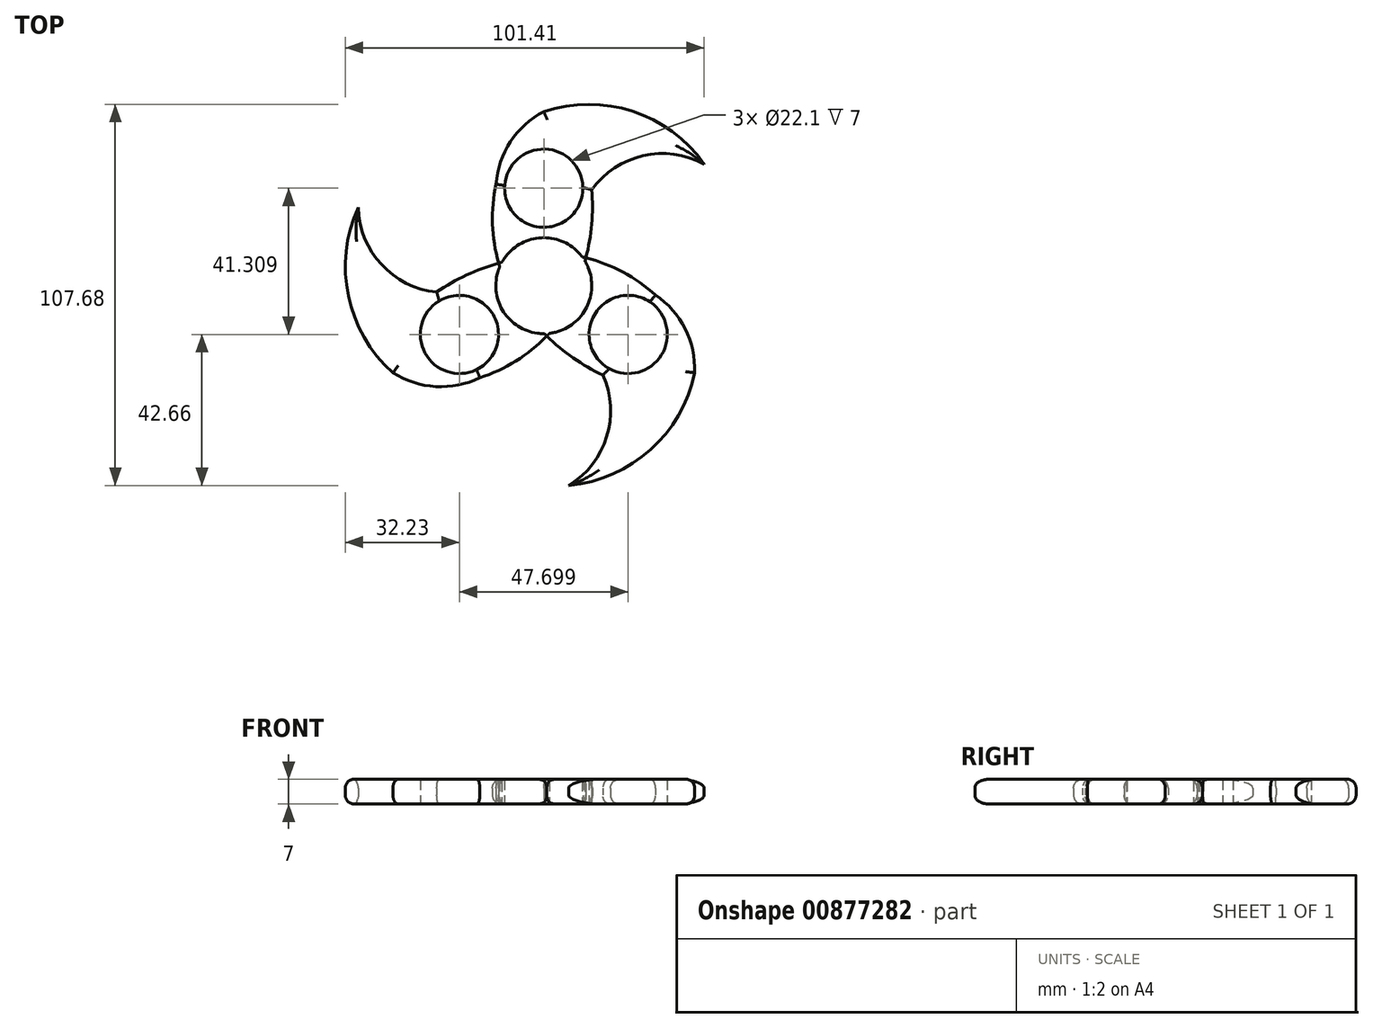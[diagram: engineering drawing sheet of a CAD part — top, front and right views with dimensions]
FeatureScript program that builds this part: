
annotation { "Feature Type Name" : "Feature", "Feature Type Description" : "" }
export const myFeature = defineFeature(function(context is Context, id is Id, definition is map)
    precondition{}
    {
        {
            var Q0;
            Q0=qCreatedBy(makeId("Top.planeOp"),FACE);
            var sketch = newSketch(context, id + "F0", { "sketchPlane" : qUnion([Q0])});
            skCircle(sketch, "E0", {"center": v(0, 0) * mm, "radius": 11.05 * mm});
            skCircle(sketch, "E1", {"center": v(0, 0) * mm, "radius": 13.55 * mm});
            skCircle(sketch, "E2", {"center": v(0, 27.54) * mm, "radius": 11.05 * mm});
            skCircle(sketch, "E3.1.1", {"center": v(-23.85, -13.77) * mm, "radius": 11.05 * mm});
            skCircle(sketch, "E4.2.2.0", {"center": v(23.85, -13.77) * mm, "radius": 11.05 * mm});
            skArc(sketch, "E5", {"start": v(45.33, 34.35) * mm, "mid": v(25.12, 49.26) * mm, "end": v(0, 49.2) * mm});
            skArc(sketch, "E6", {"start": v(45.33, 34.35) * mm, "mid": v(28.07, 36.72) * mm, "end": v(13.54, 27.1) * mm});
            skArc(sketch, "E7", {"start": v(0, 49.2) * mm, "mid": v(-9.43, 40.68) * mm, "end": v(-13.5, 28.65) * mm});
            skArc(sketch, "E8.1.0", {"start": v(-52.41, 22.08) * mm, "mid": v(-55.22, -2.88) * mm, "end": v(-42.6, -24.6) * mm});
            skArc(sketch, "E8.1.1", {"start": v(-52.41, 22.08) * mm, "mid": v(-45.84, 5.94) * mm, "end": v(-30.23, -1.82) * mm});
            skArc(sketch, "E8.2.0", {"start": v(7.08, -56.43) * mm, "mid": v(30.1, -46.39) * mm, "end": v(42.6, -24.6) * mm});
            skArc(sketch, "E8.2.1", {"start": v(7.08, -56.43) * mm, "mid": v(17.77, -42.67) * mm, "end": v(16.7, -25.27) * mm});
            skArc(sketch, "E9.1.0", {"start": v(-42.6, -24.6) * mm, "mid": v(-30.52, -28.5) * mm, "end": v(-18.06, -26.02) * mm});
            skArc(sketch, "E9.2.0", {"start": v(42.6, -24.6) * mm, "mid": v(39.95, -12.18) * mm, "end": v(31.57, -2.63) * mm});
            skArc(sketch, "E10", {"start": v(11.65, 6.92) * mm, "mid": v(13.48, 16.92) * mm, "end": v(13.54, 27.1) * mm});
            skArc(sketch, "E11", {"start": v(-13.5, 28.65) * mm, "mid": v(-14.47, 16.93) * mm, "end": v(-12.45, 5.35) * mm});
            skArc(sketch, "E12.1.0", {"start": v(-18.06, -26.02) * mm, "mid": v(-7.43, -21) * mm, "end": v(1.6, -13.46) * mm});
            skArc(sketch, "E12.1.1", {"start": v(-11.82, 6.63) * mm, "mid": v(-21.4, 3.21) * mm, "end": v(-30.23, -1.82) * mm});
            skArc(sketch, "E12.2.0", {"start": v(31.57, -2.63) * mm, "mid": v(21.9, 4.06) * mm, "end": v(10.86, 8.1) * mm});
            skArc(sketch, "E12.2.1", {"start": v(0.17, -13.55) * mm, "mid": v(7.92, -20.13) * mm, "end": v(16.7, -25.27) * mm});
            skSolve(sketch);
        }
        {
            var Q0;
            Q0=makeQuery(id+"F0.imprint","IMPRINT",FACE,{"disambiguationData":[TD([[makeQuery(id+"F0.imprint","IMPRINT",EDGE,{"derivedFrom":sQuery(id+"F0.wireOp",EDGE,"E2")}),-1.0]])]});
            var Q1;
            Q1=makeQuery(id+"F0.imprint","IMPRINT",FACE,{"disambiguationData":[TD([[makeQuery(id+"F0.imprint","IMPRINT",EDGE,{"derivedFrom":sQuery(id+"F0.wireOp",EDGE,"E4.2.2.0")}),-1.0]])]});
            var Q2;
            Q2=makeQuery(id+"F0.imprint","IMPRINT",FACE,{"disambiguationData":[TD([[makeQuery(id+"F0.imprint","IMPRINT",EDGE,{"derivedFrom":sQuery(id+"F0.wireOp",EDGE,"E3.1.1")}),-1.0]])]});
            extrude(context, id + "F1", {"entities" : qUnion([Q0, Q1, Q2]), "depth" : 7 * mm, "offsetDistance" : 25 * mm});
        }
        {
            var Q0;
            Q0=makeQuery(id+"F1.opExtrude","CAP_EDGE",EDGE,{"disambiguationData":[OSD([sQuery(id+"F0.wireOp",EDGE,"E9.1.0")])],"isStart":false});
            var Q1;
            Q1=makeQuery(id+"F1.opExtrude","CAP_EDGE",EDGE,{"disambiguationData":[OSD([sQuery(id+"F0.wireOp",EDGE,"E8.1.0")])],"isStart":false});
            var Q2;
            Q2=makeQuery(id+"F1.opExtrude","CAP_EDGE",EDGE,{"disambiguationData":[OSD([sQuery(id+"F0.wireOp",EDGE,"E8.1.1")])],"isStart":false});
            var Q3;
            {var subQ0=sQuery(id+"F0.wireOp",EDGE,"E12.1.1");Q3=makeQuery(id+"F1.opExtrude","CAP_EDGE",EDGE,{"disambiguationData":[OSD([subQ0]),TDD([makeQuery(id+"F0.imprint","IMPRINT",EDGE,{"disambiguationData":[TD([[makeQuery(id+"F0.imprint","INTERSECT",VERTEX,{"derivedFrom":[sQuery(id+"F0.wireOp",EDGE,"E8.1.1"),subQ0]}),1.0]])],"derivedFrom":subQ0})])],"isStart":false});}
            var Q4;
            {var subQ0=sQuery(id+"F0.wireOp",EDGE,"E12.1.0");Q4=makeQuery(id+"F1.opExtrude","CAP_EDGE",EDGE,{"disambiguationData":[OSD([subQ0]),TDD([makeQuery(id+"F0.imprint","IMPRINT",EDGE,{"disambiguationData":[TD([[makeQuery(id+"F0.imprint","INTERSECT",VERTEX,{"derivedFrom":[sQuery(id+"F0.wireOp",EDGE,"E9.1.0"),subQ0]}),-1.0]])],"derivedFrom":subQ0})])],"isStart":false});}
            var Q5;
            Q5=makeQuery(id+"F1.opExtrude","CAP_EDGE",EDGE,{"disambiguationData":[OSD([sQuery(id+"F0.wireOp",EDGE,"E6")])],"isStart":false});
            var Q6;
            {var subQ0=sQuery(id+"F0.wireOp",EDGE,"E10");Q6=makeQuery(id+"F1.opExtrude","CAP_EDGE",EDGE,{"disambiguationData":[OSD([subQ0]),TDD([makeQuery(id+"F0.imprint","IMPRINT",EDGE,{"disambiguationData":[TD([[makeQuery(id+"F0.imprint","INTERSECT",VERTEX,{"derivedFrom":[sQuery(id+"F0.wireOp",EDGE,"E6"),subQ0]}),1.0]])],"derivedFrom":subQ0})])],"isStart":false});}
            var Q7;
            {var subQ0=sQuery(id+"F0.wireOp",EDGE,"E11");Q7=makeQuery(id+"F1.opExtrude","CAP_EDGE",EDGE,{"disambiguationData":[OSD([subQ0]),TDD([makeQuery(id+"F0.imprint","IMPRINT",EDGE,{"disambiguationData":[TD([[makeQuery(id+"F0.imprint","INTERSECT",VERTEX,{"derivedFrom":[sQuery(id+"F0.wireOp",EDGE,"E7"),subQ0]}),-1.0]])],"derivedFrom":subQ0})])],"isStart":false});}
            var Q8;
            Q8=makeQuery(id+"F1.opExtrude","CAP_EDGE",EDGE,{"disambiguationData":[OSD([sQuery(id+"F0.wireOp",EDGE,"E7")])],"isStart":false});
            var Q9;
            Q9=makeQuery(id+"F1.opExtrude","CAP_EDGE",EDGE,{"disambiguationData":[OSD([sQuery(id+"F0.wireOp",EDGE,"E5")])],"isStart":false});
            var Q10;
            {var subQ0=sQuery(id+"F0.wireOp",EDGE,"E12.2.0");Q10=makeQuery(id+"F1.opExtrude","CAP_EDGE",EDGE,{"disambiguationData":[OSD([subQ0]),TDD([makeQuery(id+"F0.imprint","IMPRINT",EDGE,{"disambiguationData":[TD([[makeQuery(id+"F0.imprint","INTERSECT",VERTEX,{"derivedFrom":[sQuery(id+"F0.wireOp",EDGE,"E9.2.0"),subQ0]}),-1.0]])],"derivedFrom":subQ0})])],"isStart":false});}
            var Q11;
            {var subQ0=sQuery(id+"F0.wireOp",EDGE,"E12.2.1");Q11=makeQuery(id+"F1.opExtrude","CAP_EDGE",EDGE,{"disambiguationData":[OSD([subQ0]),TDD([makeQuery(id+"F0.imprint","IMPRINT",EDGE,{"disambiguationData":[TD([[makeQuery(id+"F0.imprint","INTERSECT",VERTEX,{"derivedFrom":[sQuery(id+"F0.wireOp",EDGE,"E8.2.1"),subQ0]}),1.0]])],"derivedFrom":subQ0})])],"isStart":false});}
            var Q12;
            Q12=makeQuery(id+"F1.opExtrude","CAP_EDGE",EDGE,{"disambiguationData":[OSD([sQuery(id+"F0.wireOp",EDGE,"E8.2.1")])],"isStart":false});
            var Q13;
            Q13=makeQuery(id+"F1.opExtrude","CAP_EDGE",EDGE,{"disambiguationData":[OSD([sQuery(id+"F0.wireOp",EDGE,"E8.2.0")])],"isStart":false});
            var Q14;
            Q14=makeQuery(id+"F1.opExtrude","CAP_EDGE",EDGE,{"disambiguationData":[OSD([sQuery(id+"F0.wireOp",EDGE,"E9.2.0")])],"isStart":false});
            fillet(context, id + "F2", {"entities" : qUnion([Q0, Q1, Q2, Q3, Q4, Q5, Q6, Q7, Q8, Q9, Q10, Q11, Q12, Q13, Q14]), "radius" : 2.5 * mm, "tangentPropagation" : true, "allowEdgeOverflow" : false});
        }
        {
            var Q0;
            {var subQ0=sQuery(id+"F0.wireOp",EDGE,"E12.1.0");Q0=makeQuery(id+"F1.opExtrude","CAP_EDGE",EDGE,{"disambiguationData":[OSD([subQ0]),TDD([makeQuery(id+"F0.imprint","IMPRINT",EDGE,{"disambiguationData":[TD([[makeQuery(id+"F0.imprint","INTERSECT",VERTEX,{"derivedFrom":[sQuery(id+"F0.wireOp",EDGE,"E9.1.0"),subQ0]}),-1.0]])],"derivedFrom":subQ0})])],"isStart":true});}
            var Q1;
            Q1=makeQuery(id+"F1.opExtrude","CAP_EDGE",EDGE,{"disambiguationData":[OSD([sQuery(id+"F0.wireOp",EDGE,"E9.1.0")])],"isStart":true});
            var Q2;
            Q2=makeQuery(id+"F1.opExtrude","CAP_EDGE",EDGE,{"disambiguationData":[OSD([sQuery(id+"F0.wireOp",EDGE,"E8.1.0")])],"isStart":true});
            var Q3;
            Q3=makeQuery(id+"F1.opExtrude","CAP_EDGE",EDGE,{"disambiguationData":[OSD([sQuery(id+"F0.wireOp",EDGE,"E8.1.1")])],"isStart":true});
            var Q4;
            {var subQ0=sQuery(id+"F0.wireOp",EDGE,"E12.1.1");Q4=makeQuery(id+"F1.opExtrude","CAP_EDGE",EDGE,{"disambiguationData":[OSD([subQ0]),TDD([makeQuery(id+"F0.imprint","IMPRINT",EDGE,{"disambiguationData":[TD([[makeQuery(id+"F0.imprint","INTERSECT",VERTEX,{"derivedFrom":[sQuery(id+"F0.wireOp",EDGE,"E8.1.1"),subQ0]}),1.0]])],"derivedFrom":subQ0})])],"isStart":true});}
            var Q5;
            {var subQ0=sQuery(id+"F0.wireOp",EDGE,"E11");Q5=makeQuery(id+"F1.opExtrude","CAP_EDGE",EDGE,{"disambiguationData":[OSD([subQ0]),TDD([makeQuery(id+"F0.imprint","IMPRINT",EDGE,{"disambiguationData":[TD([[makeQuery(id+"F0.imprint","INTERSECT",VERTEX,{"derivedFrom":[sQuery(id+"F0.wireOp",EDGE,"E7"),subQ0]}),-1.0]])],"derivedFrom":subQ0})])],"isStart":true});}
            var Q6;
            {var subQ0=sQuery(id+"F0.wireOp",EDGE,"E10");Q6=makeQuery(id+"F1.opExtrude","CAP_EDGE",EDGE,{"disambiguationData":[OSD([subQ0]),TDD([makeQuery(id+"F0.imprint","IMPRINT",EDGE,{"disambiguationData":[TD([[makeQuery(id+"F0.imprint","INTERSECT",VERTEX,{"derivedFrom":[sQuery(id+"F0.wireOp",EDGE,"E6"),subQ0]}),1.0]])],"derivedFrom":subQ0})])],"isStart":true});}
            var Q7;
            Q7=makeQuery(id+"F1.opExtrude","CAP_EDGE",EDGE,{"disambiguationData":[OSD([sQuery(id+"F0.wireOp",EDGE,"E6")])],"isStart":true});
            var Q8;
            Q8=makeQuery(id+"F1.opExtrude","CAP_EDGE",EDGE,{"disambiguationData":[OSD([sQuery(id+"F0.wireOp",EDGE,"E5")])],"isStart":true});
            var Q9;
            Q9=makeQuery(id+"F1.opExtrude","CAP_EDGE",EDGE,{"disambiguationData":[OSD([sQuery(id+"F0.wireOp",EDGE,"E7")])],"isStart":true});
            var Q10;
            {var subQ0=sQuery(id+"F0.wireOp",EDGE,"E12.2.0");Q10=makeQuery(id+"F1.opExtrude","CAP_EDGE",EDGE,{"disambiguationData":[OSD([subQ0]),TDD([makeQuery(id+"F0.imprint","IMPRINT",EDGE,{"disambiguationData":[TD([[makeQuery(id+"F0.imprint","INTERSECT",VERTEX,{"derivedFrom":[sQuery(id+"F0.wireOp",EDGE,"E9.2.0"),subQ0]}),-1.0]])],"derivedFrom":subQ0})])],"isStart":true});}
            var Q11;
            Q11=makeQuery(id+"F1.opExtrude","CAP_EDGE",EDGE,{"disambiguationData":[OSD([sQuery(id+"F0.wireOp",EDGE,"E9.2.0")])],"isStart":true});
            var Q12;
            Q12=makeQuery(id+"F1.opExtrude","CAP_EDGE",EDGE,{"disambiguationData":[OSD([sQuery(id+"F0.wireOp",EDGE,"E8.2.0")])],"isStart":true});
            var Q13;
            Q13=makeQuery(id+"F1.opExtrude","CAP_EDGE",EDGE,{"disambiguationData":[OSD([sQuery(id+"F0.wireOp",EDGE,"E8.2.1")])],"isStart":true});
            var Q14;
            {var subQ0=sQuery(id+"F0.wireOp",EDGE,"E12.2.1");Q14=makeQuery(id+"F1.opExtrude","CAP_EDGE",EDGE,{"disambiguationData":[OSD([subQ0]),TDD([makeQuery(id+"F0.imprint","IMPRINT",EDGE,{"disambiguationData":[TD([[makeQuery(id+"F0.imprint","INTERSECT",VERTEX,{"derivedFrom":[sQuery(id+"F0.wireOp",EDGE,"E8.2.1"),subQ0]}),1.0]])],"derivedFrom":subQ0})])],"isStart":true});}
            fillet(context, id + "F3", {"entities" : qUnion([Q0, Q1, Q2, Q3, Q4, Q5, Q6, Q7, Q8, Q9, Q10, Q11, Q12, Q13, Q14]), "radius" : 2.5 * mm, "tangentPropagation" : true, "allowEdgeOverflow" : false});
        }
    });
